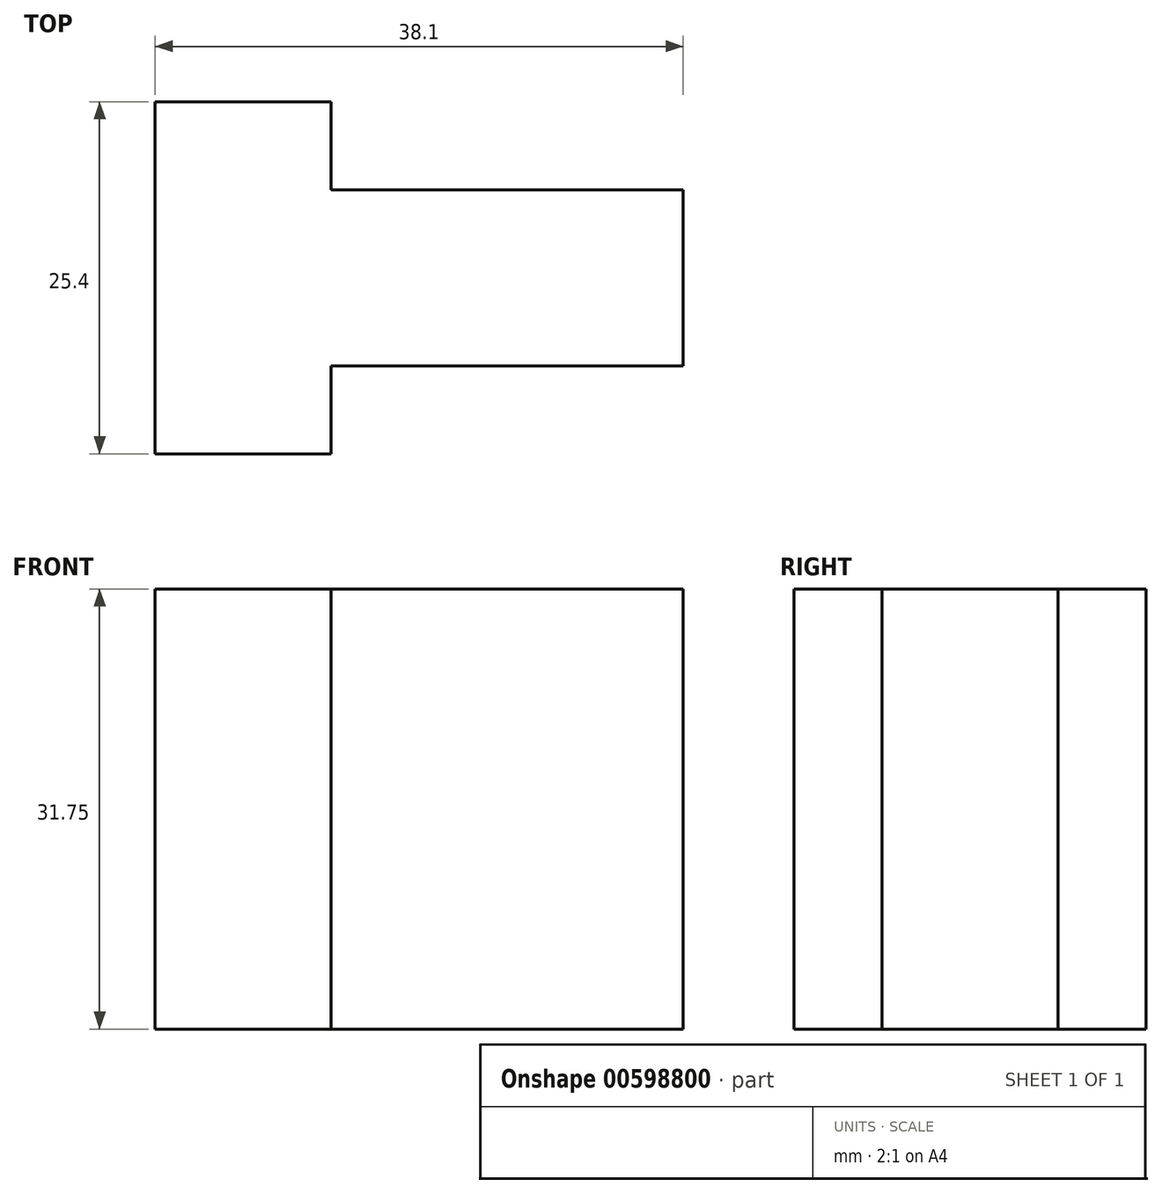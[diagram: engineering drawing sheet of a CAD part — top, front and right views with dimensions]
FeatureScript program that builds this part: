
annotation { "Feature Type Name" : "Feature", "Feature Type Description" : "" }
export const myFeature = defineFeature(function(context is Context, id is Id, definition is map)
    precondition{}
    {
        {
            var Q0;
            Q0=qCreatedBy(makeId("Front.planeOp"),FACE);
            var sketch = newSketch(context, id + "F0", { "sketchPlane" : qUnion([Q0])});
            skLineSegment(sketch, "E0", {"start": v(0, 0) * mm, "end": v(-12.7, 0) * mm});
            skLineSegment(sketch, "E1", {"start": v(-12.7, 0) * mm, "end": v(-12.7, 31.75) * mm});
            skLineSegment(sketch, "E2", {"start": v(-12.7, 31.75) * mm, "end": v(0, 31.75) * mm});
            skLineSegment(sketch, "E3", {"start": v(0, 31.75) * mm, "end": v(0, 0) * mm});
            skSolve(sketch);
        }
        {
            var Q0;
            Q0=makeQuery(id+"F0.imprint","IMPRINT",FACE,{"disambiguationData":[TD([[makeQuery(id+"F0.imprint","IMPRINT",EDGE,{"derivedFrom":sQuery(id+"F0.wireOp",EDGE,"E0")}),-1.0]])]});
            extrude(context, id + "F1", {"entities" : qUnion([Q0]), "depth" : 12.7 * mm, "offsetDistance" : 25.4 * mm});
        }
        {
            var Q0;
            Q0=makeQuery(id+"F1.opExtrude","CAP_FACE",FACE,{"disambiguationData":[OSD([sQuery(id+"F0.wireOp",EDGE,"E0"),sQuery(id+"F0.wireOp",EDGE,"E1"),sQuery(id+"F0.wireOp",EDGE,"E2"),sQuery(id+"F0.wireOp",EDGE,"E3")])],"isStart":true});
            extrude(context, id + "F2", {"entities" : qUnion([Q0]), "operationType" : NewBodyOperationType.ADD, "depth" : 12.7 * mm, "offsetDistance" : 25.4 * mm});
        }
        {
            var Q0;
            Q0=qCreatedBy(makeId("Right.planeOp"),FACE);
            var sketch = newSketch(context, id + "F3", { "sketchPlane" : qUnion([Q0])});
            skLineSegment(sketch, "E4", {"start": v(0, 0) * mm, "end": v(-6.35, 0) * mm});
            skLineSegment(sketch, "E5", {"start": v(0, 0) * mm, "end": v(6.35, 0) * mm});
            skLineSegment(sketch, "E6", {"start": v(-6.35, 0) * mm, "end": v(-6.35, 31.75) * mm});
            skLineSegment(sketch, "E7", {"start": v(6.35, 0) * mm, "end": v(6.35, 31.75) * mm});
            skLineSegment(sketch, "E8", {"start": v(-6.35, 31.75) * mm, "end": v(6.35, 31.75) * mm});
            skSolve(sketch);
        }
        {
            var Q0;
            Q0=makeQuery(id+"F3.imprint","IMPRINT",FACE,{"disambiguationData":[TD([[makeQuery(id+"F3.imprint","IMPRINT",EDGE,{"derivedFrom":sQuery(id+"F3.wireOp",EDGE,"E4")}),-1.0]])]});
            extrude(context, id + "F4", {"entities" : qUnion([Q0]), "operationType" : NewBodyOperationType.ADD, "depth" : 25.4 * mm, "offsetDistance" : 25.4 * mm});
        }
    });
